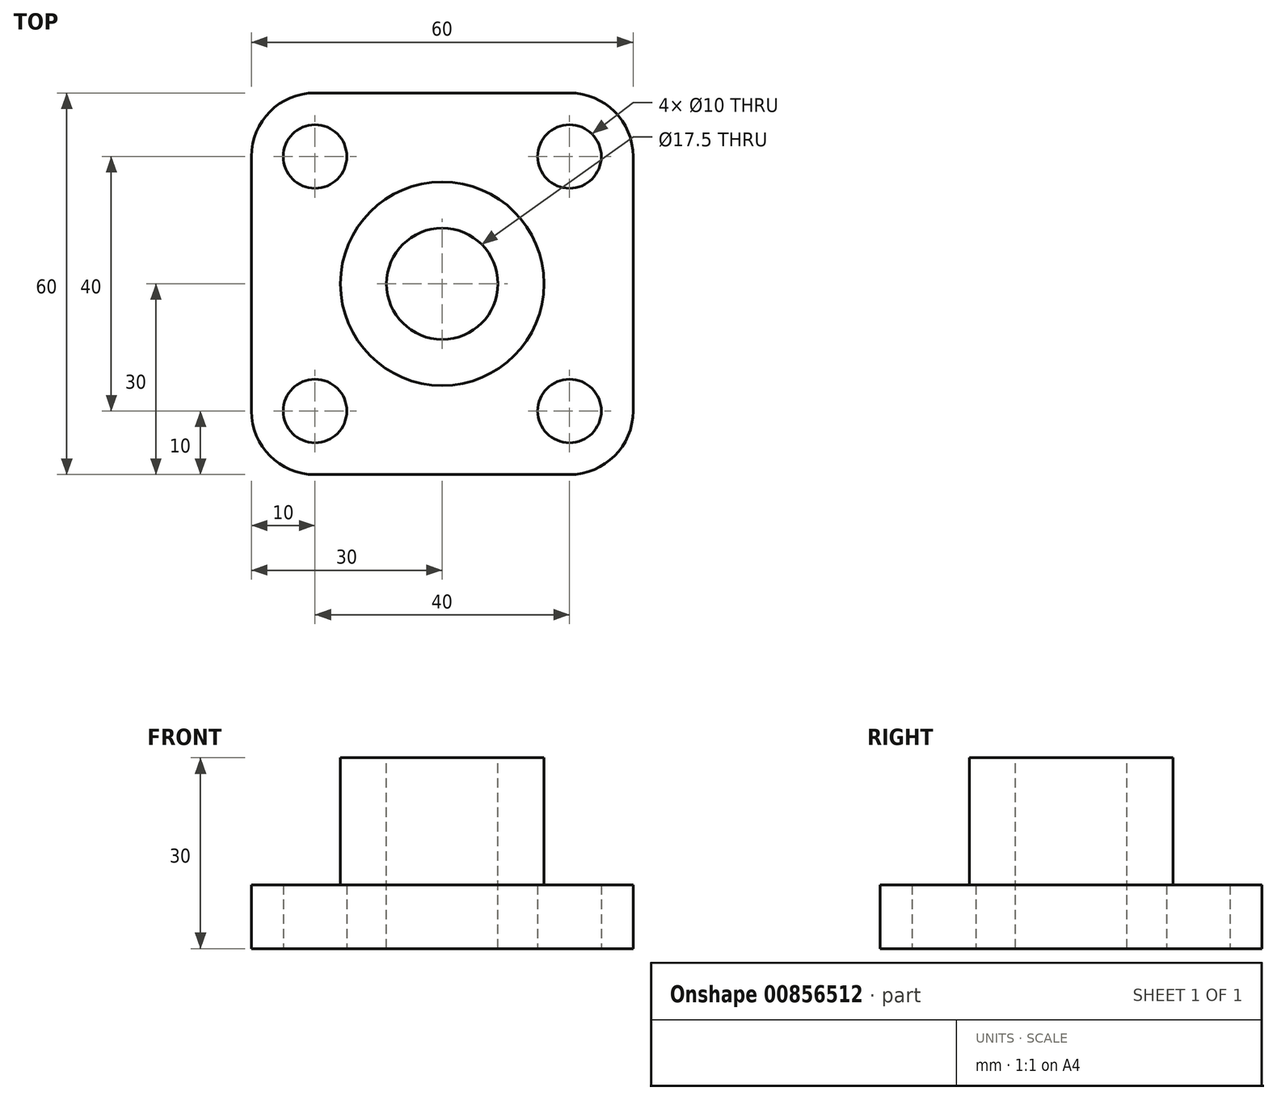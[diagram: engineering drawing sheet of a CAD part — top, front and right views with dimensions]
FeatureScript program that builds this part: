
annotation { "Feature Type Name" : "Feature", "Feature Type Description" : "" }
export const myFeature = defineFeature(function(context is Context, id is Id, definition is map)
    precondition{}
    {
        {
            var Q0;
            Q0=qCreatedBy(makeId("Top.planeOp"),FACE);
            var sketch = newSketch(context, id + "F0", { "sketchPlane" : qUnion([Q0])});
            skLineSegment(sketch, "E0.bottom", {"start": v(20, 30) * mm, "end": v(-20, 30) * mm});
            skLineSegment(sketch, "E0.top", {"start": v(20, -30) * mm, "end": v(-20, -30) * mm});
            skLineSegment(sketch, "E0.left", {"start": v(30, 20) * mm, "end": v(30, -20) * mm});
            skLineSegment(sketch, "E0.right", {"start": v(-30, 20) * mm, "end": v(-30, -20) * mm});
            skPoint(sketch, "E0.middle", {"position": v(0, 0) * mm});
            skCircle(sketch, "E1", {"center": v(0, 0) * mm, "radius": 16 * mm});
            skPoint(sketch, "E2.visualSharp", {"position": v(-30, 30) * mm});
            skArc(sketch, "E2.filletArc", {"start": v(-20, 30) * mm, "mid": v(-27.07, 27.07) * mm, "end": v(-30, 20) * mm});
            skPoint(sketch, "E3.visualSharp", {"position": v(30, 30) * mm});
            skArc(sketch, "E3.filletArc", {"start": v(30, 20) * mm, "mid": v(27.07, 27.07) * mm, "end": v(20, 30) * mm});
            skPoint(sketch, "E4.visualSharp", {"position": v(30, -30) * mm});
            skArc(sketch, "E4.filletArc", {"start": v(20, -30) * mm, "mid": v(27.07, -27.07) * mm, "end": v(30, -20) * mm});
            skPoint(sketch, "E5.visualSharp", {"position": v(-30, -30) * mm});
            skArc(sketch, "E5.filletArc", {"start": v(-30, -20) * mm, "mid": v(-27.07, -27.07) * mm, "end": v(-20, -30) * mm});
            skSolve(sketch);
        }
        {
            var Q0;
            Q0=makeQuery(id+"F0.imprint","IMPRINT",FACE,{"disambiguationData":[TD([[makeQuery(id+"F0.imprint","IMPRINT",EDGE,{"derivedFrom":sQuery(id+"F0.wireOp",EDGE,"E0.bottom")}),1.0]])]});
            var Q1;
            Q1=makeQuery(id+"F0.imprint","IMPRINT",FACE,{"disambiguationData":[TD([[makeQuery(id+"F0.imprint","IMPRINT",EDGE,{"derivedFrom":sQuery(id+"F0.wireOp",EDGE,"E1")}),1.0]])]});
            extrude(context, id + "F1", {"entities" : qUnion([Q0, Q1]), "depth" : 10 * mm, "offsetDistance" : 25 * mm});
        }
        {
            var Q0;
            Q0=sQuery(id+"F0.wireOp",VERTEX,"E2.filletArc.center");
            var Q1;
            Q1=sQuery(id+"F0.wireOp",VERTEX,"E3.filletArc.center");
            var Q2;
            Q2=sQuery(id+"F0.wireOp",VERTEX,"E4.filletArc.center");
            var Q3;
            Q3=sQuery(id+"F0.wireOp",VERTEX,"E5.filletArc.center");
            var Q4;
            Q4=makeQuery(id+"F1.opExtrude","SWEPT_BODY",BODY,{"disambiguationData":[OSD([sQuery(id+"F0.wireOp",EDGE,"E0.bottom"),sQuery(id+"F0.wireOp",EDGE,"E0.top"),sQuery(id+"F0.wireOp",EDGE,"E0.left"),sQuery(id+"F0.wireOp",EDGE,"E0.right"),sQuery(id+"F0.wireOp",EDGE,"E2.filletArc"),sQuery(id+"F0.wireOp",EDGE,"E3.filletArc"),sQuery(id+"F0.wireOp",EDGE,"E4.filletArc"),sQuery(id+"F0.wireOp",EDGE,"E5.filletArc")])]});
            hole(context, id + "F2", {"style" : HoleStyle.SIMPLE, "endStyle" : HoleEndStyle.BLIND, "oppositeDirection" : true, "holeDiameter" : 10 * mm, "majorDiameter" : 16 * mm, "holeDepth" : 10 * mm, "isTappedThrough" : true, "tappedDepth" : 25 * mm, "tapClearance" : 3, "locations" : qUnion([Q0, Q1, Q2, Q3]), "scope" : qUnion([Q4])});
        }
        {
            var Q0;
            Q0=makeQuery(id+"F1.opExtrude","CAP_FACE",FACE,{"disambiguationData":[OSD([sQuery(id+"F0.wireOp",EDGE,"E0.bottom"),sQuery(id+"F0.wireOp",EDGE,"E0.top"),sQuery(id+"F0.wireOp",EDGE,"E0.left"),sQuery(id+"F0.wireOp",EDGE,"E0.right"),sQuery(id+"F0.wireOp",EDGE,"E2.filletArc"),sQuery(id+"F0.wireOp",EDGE,"E3.filletArc"),sQuery(id+"F0.wireOp",EDGE,"E4.filletArc"),sQuery(id+"F0.wireOp",EDGE,"E5.filletArc")])],"isStart":false});
            var sketch = newSketch(context, id + "F3", { "sketchPlane" : qUnion([Q0])});
            skCircle(sketch, "E6", {"center": v(0, 0) * mm, "radius": 16 * mm});
            skSolve(sketch);
        }
        {
            var Q0;
            Q0=makeQuery(id+"F3.imprint","IMPRINT",FACE,{"disambiguationData":[TD([[makeQuery(id+"F3.imprint","IMPRINT",EDGE,{"derivedFrom":sQuery(id+"F3.wireOp",EDGE,"E6")}),1.0]])]});
            extrude(context, id + "F4", {"entities" : qUnion([Q0]), "operationType" : NewBodyOperationType.ADD, "depth" : 20 * mm, "offsetDistance" : 25 * mm});
        }
        {
            var Q0;
            Q0=makeQuery(id+"F4.opExtrude","CAP_FACE",FACE,{"disambiguationData":[OSD([sQuery(id+"F3.wireOp",EDGE,"E6")])],"isStart":false});
            var sketch = newSketch(context, id + "F5", { "sketchPlane" : qUnion([Q0])});
            skCircle(sketch, "E7", {"center": v(0, 0) * mm, "radius": 16 * mm});
            skSolve(sketch);
        }
        {
            var Q0;
            Q0=sQuery(id+"F5.wireOp",VERTEX,"E7.center");
            var Q1;
            Q1=makeQuery(id+"F1.opExtrude","SWEPT_BODY",BODY,{"disambiguationData":[OSD([sQuery(id+"F0.wireOp",EDGE,"E0.bottom"),sQuery(id+"F0.wireOp",EDGE,"E0.top"),sQuery(id+"F0.wireOp",EDGE,"E0.left"),sQuery(id+"F0.wireOp",EDGE,"E0.right"),sQuery(id+"F0.wireOp",EDGE,"E2.filletArc"),sQuery(id+"F0.wireOp",EDGE,"E3.filletArc"),sQuery(id+"F0.wireOp",EDGE,"E4.filletArc"),sQuery(id+"F0.wireOp",EDGE,"E5.filletArc")])]});
            hole(context, id + "F6", {"style" : HoleStyle.SIMPLE, "endStyle" : HoleEndStyle.THROUGH, "standardTappedOrClearance" : lookupTablePath({ "fit" : "Normal", "standard" : "ISO", "size" : "M16", "type" : "Clearance" }), "standardBlindInLast" : lookupTablePath({ "fit" : "Standard", "standard" : "ISO", "size" : "M16", "type" : "Clearance" }), "holeDiameter" : 17.5 * mm, "majorDiameter" : 5 * mm, "isTappedThrough" : true, "tappedDepth" : 25 * mm, "tapClearance" : 3, "locations" : qUnion([Q0]), "scope" : qUnion([Q1])});
        }
    });
